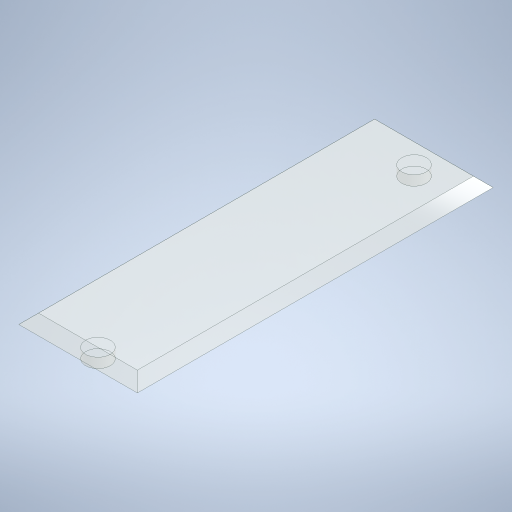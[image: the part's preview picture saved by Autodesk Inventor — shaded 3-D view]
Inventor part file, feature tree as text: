
AUTODESK INVENTOR PART (.ipt)
format: ipt  version: 2024 (Build 280153000, 153)  size: 276,480 bytes
history: native  units: in
note: dims shown in document units (in); Inventor stores cm internally (conversion verified against a paired STEP export)
features: extrude x5, sketch x5, projected_geometry x2, chamfer x1
ambient origin geometry x8: Origin, YZ Plane, XZ Plane, XY Plane, X Axis, Y Axis, Z Axis, Center Point
bodies: Solid1 (feature_tree)
feature tree (13):
  extrude  "Extrusion1"  Depth=0.1in TaperAngle=45.0deg
  chamfer  "Chamfer1"  Distance=0.1in
  extrude  "Extrusion2"  Depth=0.1in TaperAngle=0.0deg
  extrude  "Extrusion3"  [1 undecoded]
  extrude  "Extrusion4"  [1 undecoded]
  extrude  "Extrusion5"  [1 undecoded]
  sketch  "Sketch1"  dims[d0=0.1in d1=0.0in d2=0.1in d3=0.125in d4=45.0deg d5=0.1in d6=0.0in]
  sketch  "Sketch2"  dims[d7=0.1in d8=0.0in d9=0.1in d10=0.0in]
  sketch  "Sketch3"  dims[d11=0.1in d12=0.0in]
  projected_geometry  "Projected Loop1"
  projected_geometry  "Projected Loop2"
  sketch  "Sketch4"
  sketch  "Sketch5"
note: 3 required parameter values undecoded (feature->parameter linkage not recoverable at this tier; creation-order binding heuristic only, values carry confidence <= 0.55)
